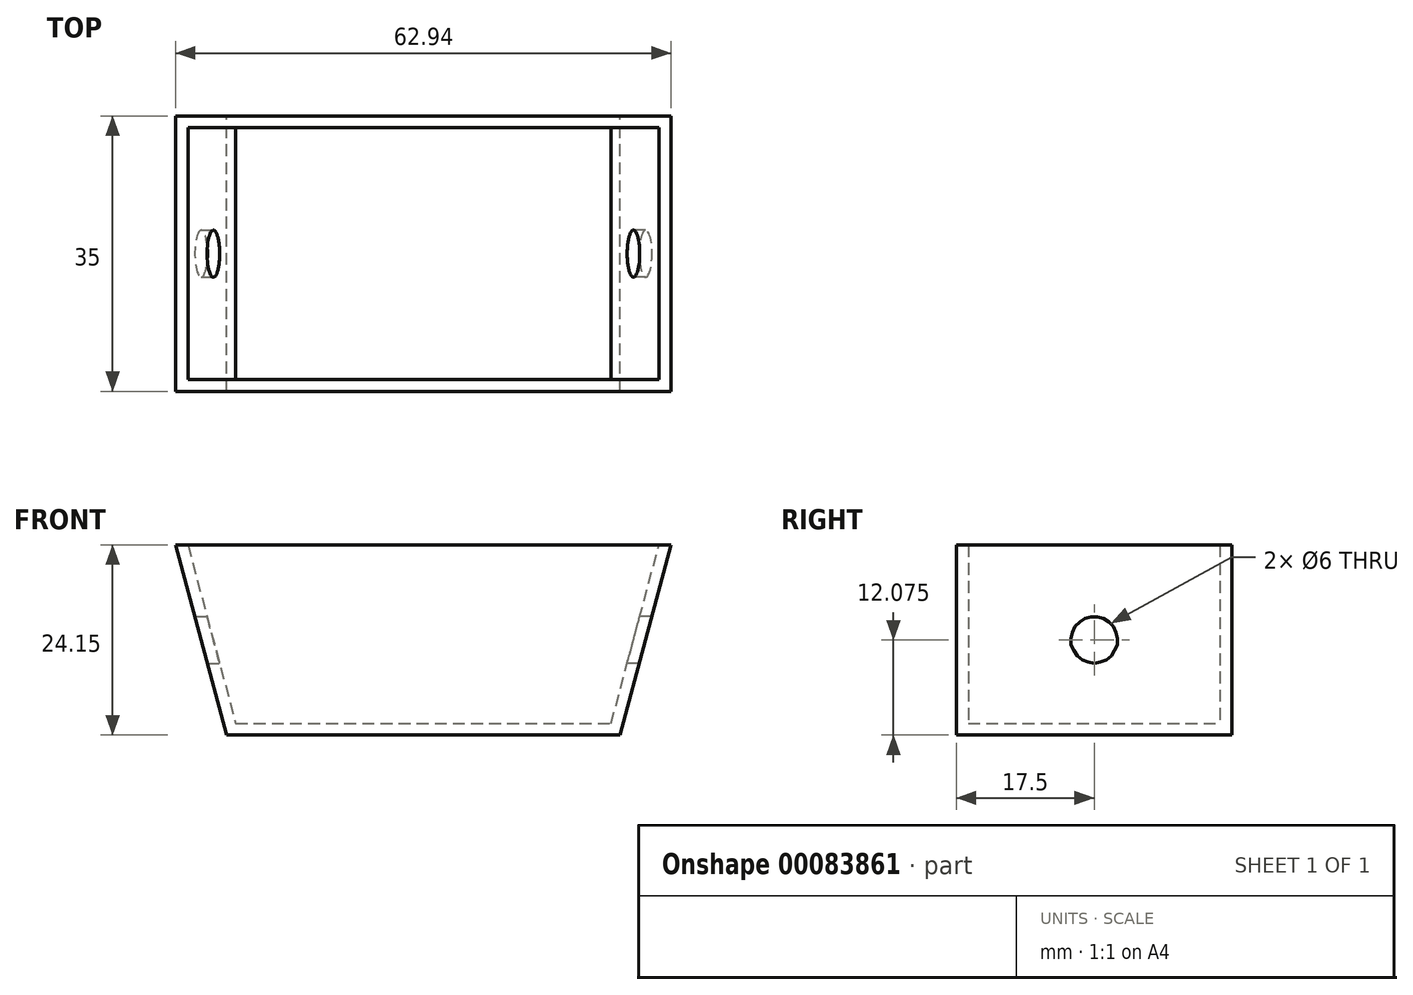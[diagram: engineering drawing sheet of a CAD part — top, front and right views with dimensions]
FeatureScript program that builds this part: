
annotation { "Feature Type Name" : "Feature", "Feature Type Description" : "" }
export const myFeature = defineFeature(function(context is Context, id is Id, definition is map)
    precondition{}
    {
        {
            var Q0;
            Q0=qCreatedBy(makeId("Front.planeOp"),FACE);
            var sketch = newSketch(context, id + "F0", { "sketchPlane" : qUnion([Q0])});
            skPoint(sketch, "E0.middle", {"position": v(0, 0) * mm});
            skLineSegment(sketch, "E1", {"start": v(-25, 24.26) * mm, "end": v(25, 24.26) * mm});
            skLineSegment(sketch, "E2", {"start": v(25, 24.26) * mm, "end": v(31.47, 48.4) * mm});
            skLineSegment(sketch, "E3", {"start": v(31.47, 48.4) * mm, "end": v(-31.47, 48.4) * mm});
            skLineSegment(sketch, "E4", {"start": v(-31.47, 48.4) * mm, "end": v(-25, 24.26) * mm});
            skSolve(sketch);
        }
        {
            var Q0;
            Q0 = qSketchRegion(id + "F0", true);
            extrude(context, id + "F1", {"entities" : qUnion([Q0]), "depth" : 35 * mm});
        }
        {
            var Q0;
            Q0=makeQuery(id+"F1.opExtrude","SWEPT_FACE",FACE,{"disambiguationData":[OSD([sQuery(id+"F0.wireOp",EDGE,"E3")])]});
            shell(context, id + "F2", {"entities" : qUnion([Q0]), "thickness" : 1.5 * mm});
        }
        {
            var Q0;
            Q0=qCreatedBy(makeId("Right.planeOp"),FACE);
            var sketch = newSketch(context, id + "F3", { "sketchPlane" : qUnion([Q0])});
            skPoint(sketch, "E5", {"position": v(-17.5, 36.34) * mm});
            skSolve(sketch);
        }
        {
            var Q0;
            Q0=sQuery(id+"F3.wireOp",VERTEX,"E5");
            var Q1;
            Q1=makeQuery(id+"F1.opExtrude","SWEPT_BODY",BODY,{"disambiguationData":[OSD([sQuery(id+"F0.wireOp",EDGE,"E1"),sQuery(id+"F0.wireOp",EDGE,"E2"),sQuery(id+"F0.wireOp",EDGE,"E3"),sQuery(id+"F0.wireOp",EDGE,"E4")])]});
            hole(context, id + "F4", {"style" : HoleStyle.SIMPLE, "endStyle" : HoleEndStyle.THROUGH, "holeDiameter" : 6 * mm, "locations" : qUnion([Q0]), "scope" : qUnion([Q1]), "isTappedThrough" : true});
        }
        {
            var Q0;
            Q0=sQuery(id+"F3.wireOp",VERTEX,"E5");
            var Q1;
            Q1=makeQuery(id+"F1.opExtrude","SWEPT_BODY",BODY,{"disambiguationData":[OSD([sQuery(id+"F0.wireOp",EDGE,"E1"),sQuery(id+"F0.wireOp",EDGE,"E2"),sQuery(id+"F0.wireOp",EDGE,"E3"),sQuery(id+"F0.wireOp",EDGE,"E4")])]});
            hole(context, id + "F5", {"style" : HoleStyle.SIMPLE, "endStyle" : HoleEndStyle.THROUGH, "oppositeDirection" : true, "holeDiameter" : 6 * mm, "locations" : qUnion([Q0]), "scope" : qUnion([Q1]), "isTappedThrough" : true});
        }
    });
